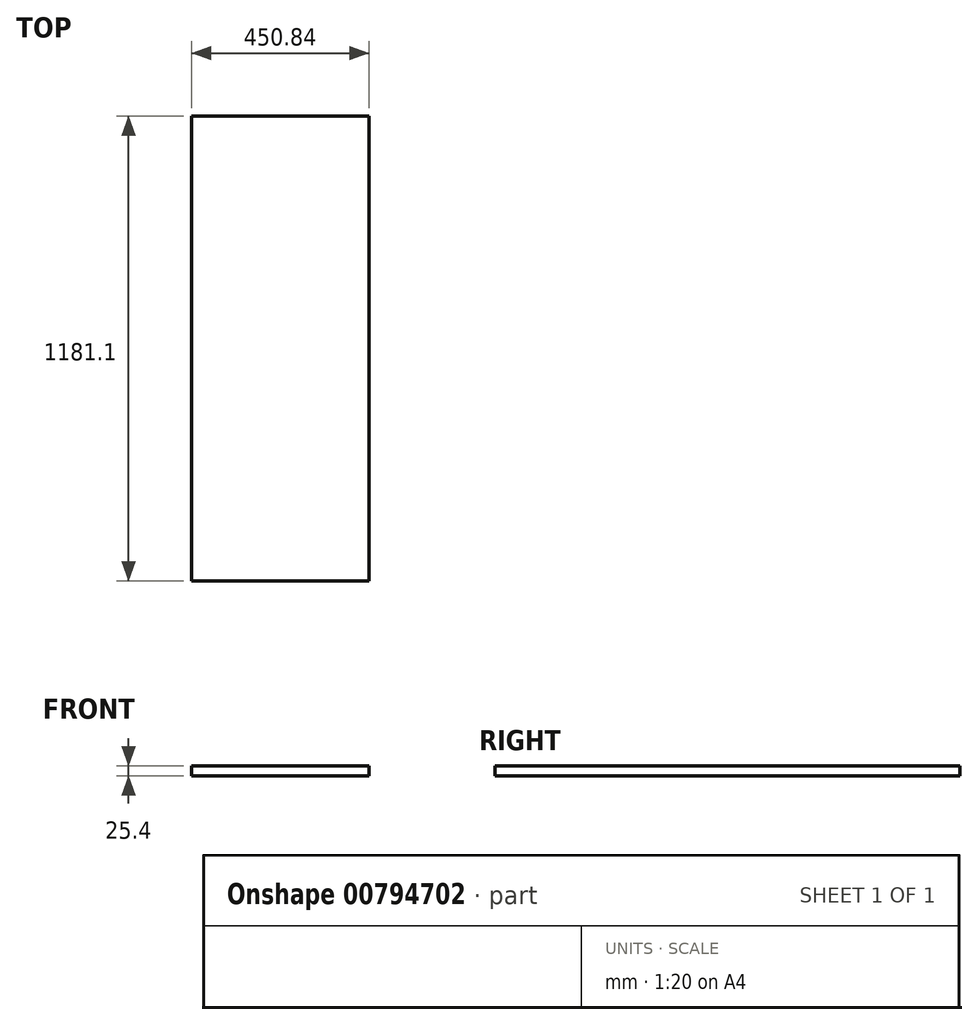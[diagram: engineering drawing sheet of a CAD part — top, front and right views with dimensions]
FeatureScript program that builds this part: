
annotation { "Feature Type Name" : "Feature", "Feature Type Description" : "" }
export const myFeature = defineFeature(function(context is Context, id is Id, definition is map)
    precondition{}
    {
        {
            var Q0;
            Q0=qCreatedBy(makeId("Top.planeOp"),FACE);
            var sketch = newSketch(context, id + "F0", { "sketchPlane" : qUnion([Q0])});
            skLineSegment(sketch, "E0.bottom", {"start": v(-225.42, -590.55) * mm, "end": v(225.43, -590.55) * mm});
            skLineSegment(sketch, "E0.top", {"start": v(-225.43, 590.55) * mm, "end": v(225.42, 590.55) * mm});
            skLineSegment(sketch, "E0.left", {"start": v(-225.42, -590.55) * mm, "end": v(-225.43, 590.55) * mm});
            skLineSegment(sketch, "E0.right", {"start": v(225.43, -590.55) * mm, "end": v(225.42, 590.55) * mm});
            skPoint(sketch, "E0.middle", {"position": v(0, 0) * mm});
            skSolve(sketch);
        }
        {
            var Q0;
            Q0=makeQuery(id+"F0.imprint","IMPRINT",FACE,{"disambiguationData":[TD([[makeQuery(id+"F0.imprint","IMPRINT",EDGE,{"derivedFrom":sQuery(id+"F0.wireOp",EDGE,"E0.bottom")}),1.0]])]});
            extrude(context, id + "F1", {"entities" : qUnion([Q0]), "depth" : 25.4 * mm, "offsetDistance" : 25.4 * mm});
        }
    });
